# Revit family: Toilet-Floor_Mount-KOHLER-Betello_Comfort_Height-K-20198_1
name_source: partatom
category: Plumbing Fixtures
revit_build: Autodesk Revit 2017 (Build: 20160225_1515(x64)
units: mm (PartAtom-declared; Revit-internal decimal feet)

## family parameters
Cut with Voids When Loaded = No
Host = Face
OmniClass Number = 23.31.19.00
OmniClass Title = Toilets
Part Type = Normal
Room Calculation Point = No
Round Connector Dimension = Use Diameter
Shared = No

## types (6) — shared parameters
ADA Compliant = Yes
Assembly Code = D2010100
CW Connection = Yes
Cold Water Inlet = Cold Water Inlet
Date Modified = 04/10/2020
Default Elevation = 0"
Description = Two-piece elongated 1.28 gpf chair height toilet with ContinuousClean Technology
Flow Rate = 0 GPM
Flush Rate- GPF = 1.28 GPF
Flush Rate- LPF = 4.8 LPF
HW Connection = No
Height = 31 3/4"
Hot Water Inlet = Hot Water Inlet
Length = 28 7/16"
Manufacturer = KOHLER Co.
Master Format 2014 = 22 42 13.13
Master Format 2014 Name = Residential Water Closets
Material = Vitreous China
Pressure = 80.00 psi
Product Documentation Link = https://www.us.kohler.com
Product Name = Betello Comfort Height
Product Page URL = http://www.us.kohler.com
Rough-In = 12"
Seat Included = No
URL = https://www.us.kohler.com
Vent Connection = No
Waste Connection = Yes
Waste Water Outlet = Waste Water Outlet
WaterSense Certified = Yes
Width = 16 5/16"

## per-type parameters (varying)
| type | Finish | Model | Type |
| 0 - White | Kohler-Vitreous_China-0-White | K-20198-0 | 1 |
| 96 - Biscuit | Kohler-Vitreous_China-96-Biscuit | K-20198-96 | 2 |
| NY - Dune | Kohler-Vitreous_China-NY-Dune | K-20198-NY | 3 |
| 95 - Ice Grey | Kohler-Vitreous_China-95-Ice_Grey | K-20198-95 | 4 |
| G9 - Sandbar | Kohler-Vitreous_China-G9-Sandbar | K-20198-G9 | 5 |
| 7 - Black Black | Kohler-Vitreous_China-7-Black_Black | K-20198-7 | 6 |

## geometry (parser evidence)
native form markers: Sweep x5
no freeform markers — native parametric forms only
